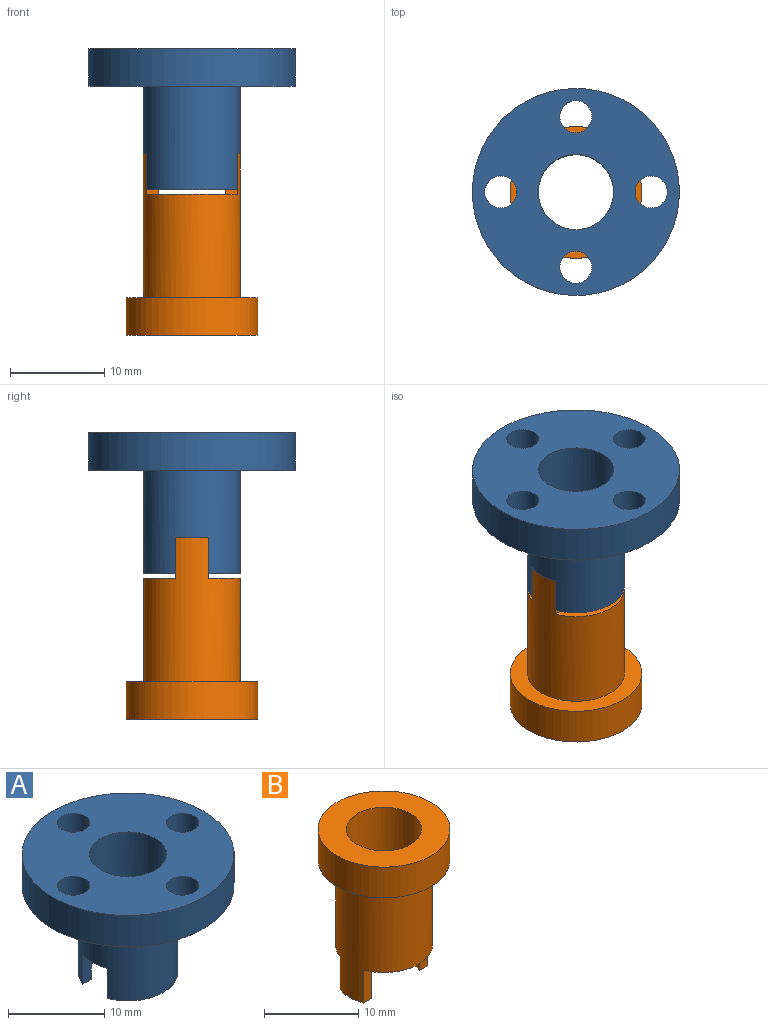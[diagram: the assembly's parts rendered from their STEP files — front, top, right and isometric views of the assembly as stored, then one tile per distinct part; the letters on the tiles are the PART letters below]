
ASSEMBLY  parts=2 mates=1
PART A: 17 faces, bbox 22x22x15 mm
  f0: plane 3.8x1.25mm, normal (0,1,0), area 4.8mm2, adj f3,f7,f11,f12
  f1: plane 3.8x1.25mm, normal (0,-1,0), area 4.8mm2, adj f7,f8,f11,f12
  f2: plane 3.6x1.58mm, normal (0,0,-1), area 4.3mm2, adj f7,f9,f10,f12
  f3: plane 9.65x3.35mm, normal (0,0,-1), area 12.3mm2, adj f0,f7,f9,f12
  f4: cylinder r=11mm len=22mm, axis (0,0,-1), area 276.5mm2, adj f5,f6
  f5: plane 22x22mm, normal (0,0,1), area 293.6mm2, adj f4,f12,f13,f14,f15,f16
  f6: plane 22x22mm, normal (0,0,-1), area 260.5mm2, adj f4,f7,f13,f14,f15,f16
  f7: cylinder r=5.15mm len=11mm, axis (0,0,1), area 328mm2, adj f0,f1,f2,f3,f6,f8,f9,f10
  f8: plane 9.65x3.35mm, normal (0,0,-1), area 12.3mm2, adj f1,f7,f10,f12
  f9: plane 3.8x1.25mm, normal (0,1,0), area 4.8mm2, adj f2,f3,f7,f12
  f10: plane 3.8x1.25mm, normal (0,-1,0), area 4.8mm2, adj f2,f7,f8,f12
  f11: plane 3.6x1.58mm, normal (0,0,-1), area 4.3mm2, adj f0,f1,f7,f12
  f12: cylinder r=4mm len=15mm, axis (0,0,1), area 348.6mm2, adj f0,f1,f2,f3,f5,f8,f9,f10
  f13: cylinder r=1.7mm len=4mm, axis (0,0,1), area 42.7mm2, adj f5,f6
  f14: cylinder r=1.7mm len=4mm, axis (0,0,1), area 42.7mm2, adj f5,f6
  f15: cylinder r=1.7mm len=4mm, axis (0,0,1), area 42.7mm2, adj f5,f6
  f16: cylinder r=1.7mm len=4mm, axis (0,0,1), area 42.7mm2, adj f5,f6
PART B: 13 faces, bbox 14x14x19.3 mm
  f0: plane 4.3x1.25mm, normal (0,-1,0), area 5.4mm2, adj f2,f3,f7,f12
  f1: plane 4.3x1.25mm, normal (0,1,0), area 5.4mm2, adj f2,f7,f8,f12
  f2: plane 3.5x1.55mm, normal (0,0,-1), area 4.1mm2, adj f0,f1,f7,f12
  f3: plane 9.69x3.4mm, normal (0,0,-1), area 12.4mm2, adj f0,f7,f9,f12
  f4: cylinder r=7mm len=14mm, axis (0,0,-1), area 175.9mm2, adj f5,f6
  f5: plane 14x14mm, normal (0,0,1), area 103.7mm2, adj f4,f12
  f6: plane 14x14mm, normal (0,0,-1), area 70.6mm2, adj f4,f7
  f7: cylinder r=5.15mm len=15.3mm, axis (0,0,1), area 386.7mm2, adj f0,f1,f2,f3,f6,f8,f9,f10
  f8: plane 9.69x3.4mm, normal (0,0,-1), area 12.4mm2, adj f1,f7,f10,f12
  f9: plane 4.3x1.25mm, normal (0,-1,0), area 5.4mm2, adj f3,f7,f11,f12
  f10: plane 4.3x1.25mm, normal (0,1,0), area 5.4mm2, adj f7,f8,f11,f12
  f11: plane 3.5x1.55mm, normal (0,0,-1), area 4.1mm2, adj f7,f9,f10,f12
  f12: cylinder r=4mm len=19.3mm, axis (0,0,1), area 408.1mm2, adj f0,f1,f2,f3,f5,f8,f9,f10
PLACE A t=(0,0,-4)mm
PLACE B rot(axis=(1,0,0),180deg) t=(0,0,-26.5)mm
MATE fastened B.f12 <-> A.f7  axis (0,0,-1) through (0,0,-11.2)mm
